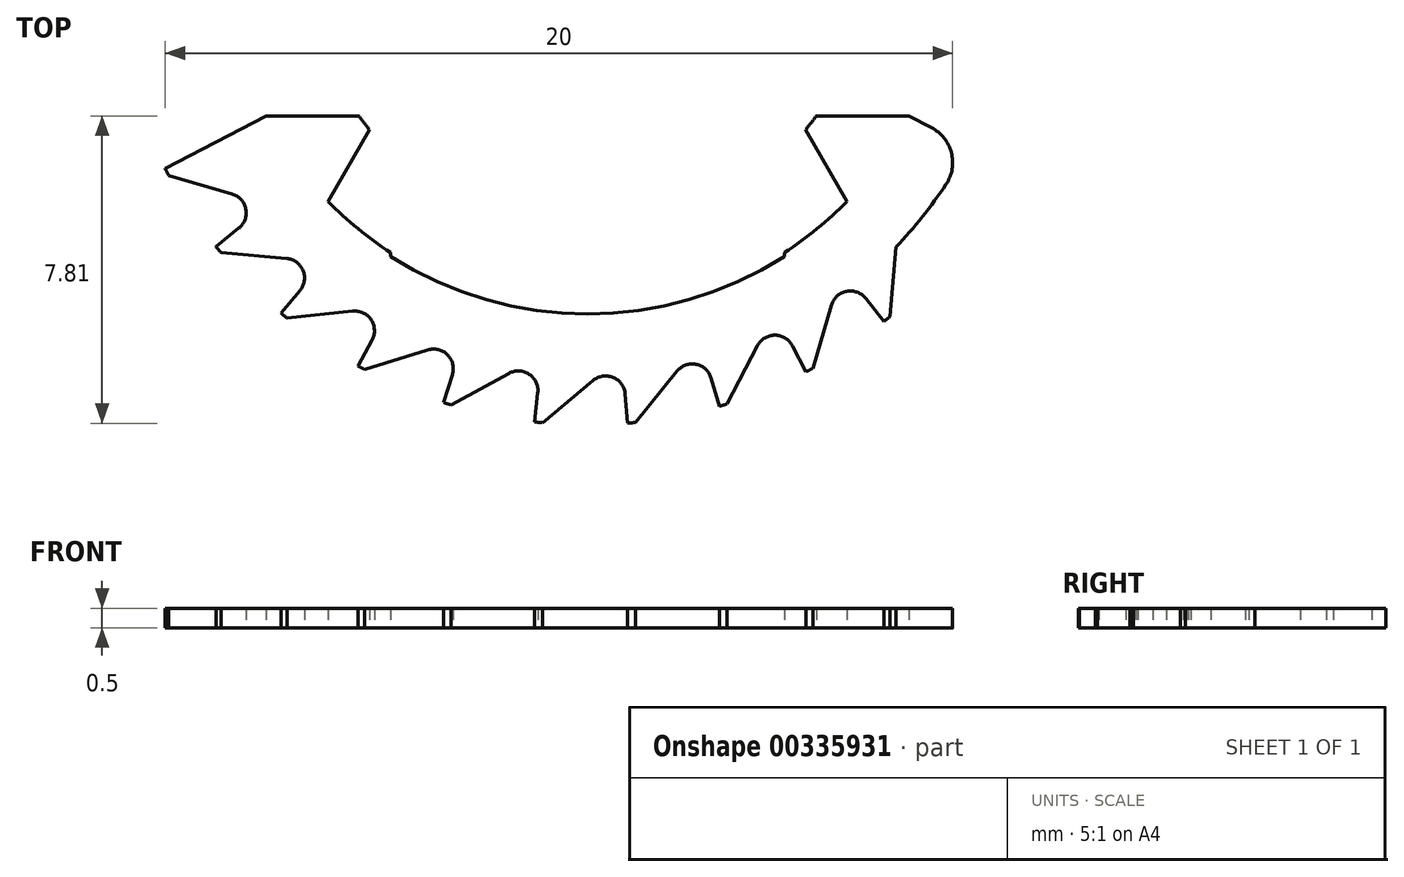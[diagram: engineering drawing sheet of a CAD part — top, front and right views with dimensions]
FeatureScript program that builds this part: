
annotation { "Feature Type Name" : "Feature", "Feature Type Description" : "" }
export const myFeature = defineFeature(function(context is Context, id is Id, definition is map)
    precondition{}
    {
        {
            var Q0;
            Q0=qCreatedBy(makeId("Top.planeOp"),FACE);
            var sketch = newSketch(context, id + "F0", { "sketchPlane" : qUnion([Q0])});
            skArc(sketch, "E0", {"start": v(-8.16, -4.25) * mm, "mid": v(0, -9.2) * mm, "end": v(8.16, -4.25) * mm, "construction": true});
            skPoint(sketch, "E1", {"position": v(0, -9.2) * mm});
            skLineSegment(sketch, "E2", {"start": v(-8.16, -4.25) * mm, "end": v(0, 0) * mm, "construction": true});
            skLineSegment(sketch, "E3", {"start": v(8.16, -4.25) * mm, "end": v(0, 0) * mm, "construction": true});
            skLineSegment(sketch, "E4", {"start": v(-8.16, -4.25) * mm, "end": v(-10.73, -5.59) * mm});
            skLineSegment(sketch, "E5", {"start": v(-8.16, -4.25) * mm, "end": v(-5.34, -4.25) * mm});
            skLineSegment(sketch, "E6", {"start": v(-5.34, -4.25) * mm, "end": v(-6.6, -6.42) * mm});
            skLineSegment(sketch, "E7", {"start": v(8.16, -4.25) * mm, "end": v(5.34, -4.25) * mm});
            skLineSegment(sketch, "E8", {"start": v(5.34, -4.25) * mm, "end": v(6.6, -6.42) * mm});
            skLineSegment(sketch, "E9", {"start": v(-6.6, -6.42) * mm, "end": v(6.6, -6.42) * mm, "construction": true});
            skPoint(sketch, "E10", {"position": v(0, -6.42) * mm});
            skArc(sketch, "E11", {"start": v(5.81, -4.25) * mm, "mid": v(5.68, -4.43) * mm, "end": v(5.54, -4.6) * mm});
            skArc(sketch, "E12", {"start": v(-5.54, -4.6) * mm, "mid": v(-5.68, -4.43) * mm, "end": v(-5.81, -4.25) * mm});
            skLineSegment(sketch, "E13", {"start": v(-5, -7.72) * mm, "end": v(5, -7.72) * mm, "construction": true});
            skArc(sketch, "E14", {"start": v(-5, -7.72) * mm, "mid": v(-5.83, -7.12) * mm, "end": v(-6.6, -6.42) * mm});
            skArc(sketch, "E15", {"start": v(6.6, -6.42) * mm, "mid": v(5.83, -7.12) * mm, "end": v(5, -7.72) * mm});
            skLineSegment(sketch, "E16", {"start": v(-5, -7.72) * mm, "end": v(-5, -7.82) * mm});
            skLineSegment(sketch, "E17", {"start": v(5, -7.72) * mm, "end": v(5, -7.82) * mm});
            skArc(sketch, "E18", {"start": v(-5, -7.82) * mm, "mid": v(0, -9.28) * mm, "end": v(5, -7.82) * mm});
            skLineSegment(sketch, "E19", {"start": v(8.16, -4.25) * mm, "end": v(9.67, -5.03) * mm});
            skArc(sketch, "E20", {"start": v(9.67, -5.03) * mm, "mid": v(0, -10.9) * mm, "end": v(-9.67, -5.03) * mm, "construction": true});
            skArc(sketch, "E21", {"start": v(-10.73, -5.59) * mm, "mid": v(0, -12.1) * mm, "end": v(10.73, -5.59) * mm, "construction": true});
            skLineSegment(sketch, "E22", {"start": v(0, 0) * mm, "end": v(9.3, -7.73) * mm, "construction": true});
            skLineSegment(sketch, "E23", {"start": v(7.83, -7.58) * mm, "end": v(7.69, -9.34) * mm});
            skArc(sketch, "E24", {"start": v(7.69, -9.34) * mm, "mid": v(7.61, -9.4) * mm, "end": v(7.53, -9.47) * mm});
            skLineSegment(sketch, "E25", {"start": v(7.53, -9.47) * mm, "end": v(7.07, -8.89) * mm});
            skArc(sketch, "E26", {"start": v(7.07, -8.89) * mm, "mid": v(6.58, -8.7) * mm, "end": v(6.2, -9.06) * mm});
            skArc(sketch, "E27", {"start": v(9.67, -5.03) * mm, "mid": v(8.84, -6.37) * mm, "end": v(7.83, -7.58) * mm});
            skLineSegment(sketch, "E28", {"start": v(6.2, -9.06) * mm, "end": v(5.72, -10.66) * mm});
            skLineSegment(sketch, "E29", {"start": v(7.07, -8.89) * mm, "end": v(0, 0) * mm, "construction": true});
            skLineSegment(sketch, "E30.1.0", {"start": v(4.32, -10.09) * mm, "end": v(3.54, -11.57) * mm});
            skArc(sketch, "E30.1.1", {"start": v(5.2, -10.1) * mm, "mid": v(4.76, -9.82) * mm, "end": v(4.32, -10.09) * mm});
            skLineSegment(sketch, "E30.1.2", {"start": v(5.55, -10.75) * mm, "end": v(5.2, -10.1) * mm});
            skArc(sketch, "E30.1.3", {"start": v(5.72, -10.66) * mm, "mid": v(5.63, -10.7) * mm, "end": v(5.55, -10.75) * mm});
            skLineSegment(sketch, "E30.2.0", {"start": v(2.27, -10.74) * mm, "end": v(1.22, -12.04) * mm});
            skArc(sketch, "E30.2.1", {"start": v(3.14, -10.91) * mm, "mid": v(2.76, -10.56) * mm, "end": v(2.27, -10.74) * mm});
            skLineSegment(sketch, "E30.2.2", {"start": v(3.35, -11.63) * mm, "end": v(3.14, -10.91) * mm});
            skArc(sketch, "E30.2.3", {"start": v(3.54, -11.57) * mm, "mid": v(3.44, -11.6) * mm, "end": v(3.35, -11.63) * mm});
            skLineSegment(sketch, "E30.3.0", {"start": v(0.14, -10.97) * mm, "end": v(-1.15, -12.05) * mm});
            skArc(sketch, "E30.3.1", {"start": v(0.96, -11.31) * mm, "mid": v(0.65, -10.9) * mm, "end": v(0.14, -10.97) * mm});
            skLineSegment(sketch, "E30.3.2", {"start": v(1.02, -12.06) * mm, "end": v(0.96, -11.31) * mm});
            skArc(sketch, "E30.3.3", {"start": v(1.22, -12.04) * mm, "mid": v(1.12, -12.05) * mm, "end": v(1.02, -12.06) * mm});
            skLineSegment(sketch, "E30.4.0", {"start": v(-2, -10.8) * mm, "end": v(-3.47, -11.6) * mm});
            skArc(sketch, "E30.4.1", {"start": v(-1.26, -11.28) * mm, "mid": v(-1.48, -10.81) * mm, "end": v(-2, -10.8) * mm});
            skLineSegment(sketch, "E30.4.2", {"start": v(-1.35, -12.02) * mm, "end": v(-1.26, -11.28) * mm});
            skArc(sketch, "E30.4.3", {"start": v(-1.15, -12.05) * mm, "mid": v(-1.25, -12.04) * mm, "end": v(-1.35, -12.02) * mm});
            skLineSegment(sketch, "E30.5.0", {"start": v(-4.06, -10.2) * mm, "end": v(-5.66, -10.7) * mm});
            skArc(sketch, "E30.5.1", {"start": v(-3.44, -10.82) * mm, "mid": v(-3.56, -10.32) * mm, "end": v(-4.06, -10.2) * mm});
            skLineSegment(sketch, "E30.5.2", {"start": v(-3.66, -11.53) * mm, "end": v(-3.44, -10.82) * mm});
            skArc(sketch, "E30.5.3", {"start": v(-3.47, -11.6) * mm, "mid": v(-3.57, -11.56) * mm, "end": v(-3.66, -11.53) * mm});
            skLineSegment(sketch, "E30.6.0", {"start": v(-5.97, -9.2) * mm, "end": v(-7.63, -9.39) * mm});
            skArc(sketch, "E30.6.1", {"start": v(-5.48, -9.95) * mm, "mid": v(-5.5, -9.43) * mm, "end": v(-5.97, -9.2) * mm});
            skLineSegment(sketch, "E30.6.2", {"start": v(-5.84, -10.6) * mm, "end": v(-5.48, -9.95) * mm});
            skArc(sketch, "E30.6.3", {"start": v(-5.66, -10.7) * mm, "mid": v(-5.75, -10.65) * mm, "end": v(-5.84, -10.6) * mm});
            skLineSegment(sketch, "E30.7.0", {"start": v(-7.65, -7.87) * mm, "end": v(-9.31, -7.72) * mm});
            skArc(sketch, "E30.7.1", {"start": v(-7.3, -8.7) * mm, "mid": v(-7.23, -8.18) * mm, "end": v(-7.65, -7.87) * mm});
            skLineSegment(sketch, "E30.7.2", {"start": v(-7.79, -9.26) * mm, "end": v(-7.3, -8.7) * mm});
            skArc(sketch, "E30.7.3", {"start": v(-7.63, -9.39) * mm, "mid": v(-7.7, -9.33) * mm, "end": v(-7.79, -9.26) * mm});
            skLineSegment(sketch, "E30.8.0", {"start": v(-9.03, -6.23) * mm, "end": v(-10.64, -5.76) * mm});
            skArc(sketch, "E30.8.1", {"start": v(-8.86, -7.1) * mm, "mid": v(-8.68, -6.62) * mm, "end": v(-9.03, -6.23) * mm});
            skLineSegment(sketch, "E30.8.2", {"start": v(-9.44, -7.57) * mm, "end": v(-8.86, -7.1) * mm});
            skArc(sketch, "E30.8.3", {"start": v(-9.31, -7.72) * mm, "mid": v(-9.38, -7.65) * mm, "end": v(-9.44, -7.57) * mm});
            skLineSegment(sketch, "E30.anchor1", {"start": v(0, 0) * mm, "end": v(5.72, -10.66) * mm, "construction": true});
            skLineSegment(sketch, "E30.anchor2", {"start": v(0, 0) * mm, "end": v(-10.64, -5.76) * mm, "construction": true});
            skArc(sketch, "E31", {"start": v(-10.73, -5.59) * mm, "mid": v(-10.69, -5.68) * mm, "end": v(-10.64, -5.76) * mm});
            skArc(sketch, "E32", {"start": v(9.11, -5.98) * mm, "mid": v(9.24, -5.18) * mm, "end": v(8.74, -4.55) * mm});
            skSolve(sketch);
        }
        {
            var Q0;
            {var subQ5=sQuery(id+"F0.wireOp",EDGE,"E4");Q0=makeQuery(id+"F0.imprint","IMPRINT",FACE,{"disambiguationData":[TD([[makeQuery(id+"F0.imprint","IMPRINT",EDGE,{"derivedFrom":subQ5}),1.0]])]});}
            extrude(context, id + "F1", {"entities" : qUnion([Q0]), "depth" : 0.5 * mm});
        }
    });
